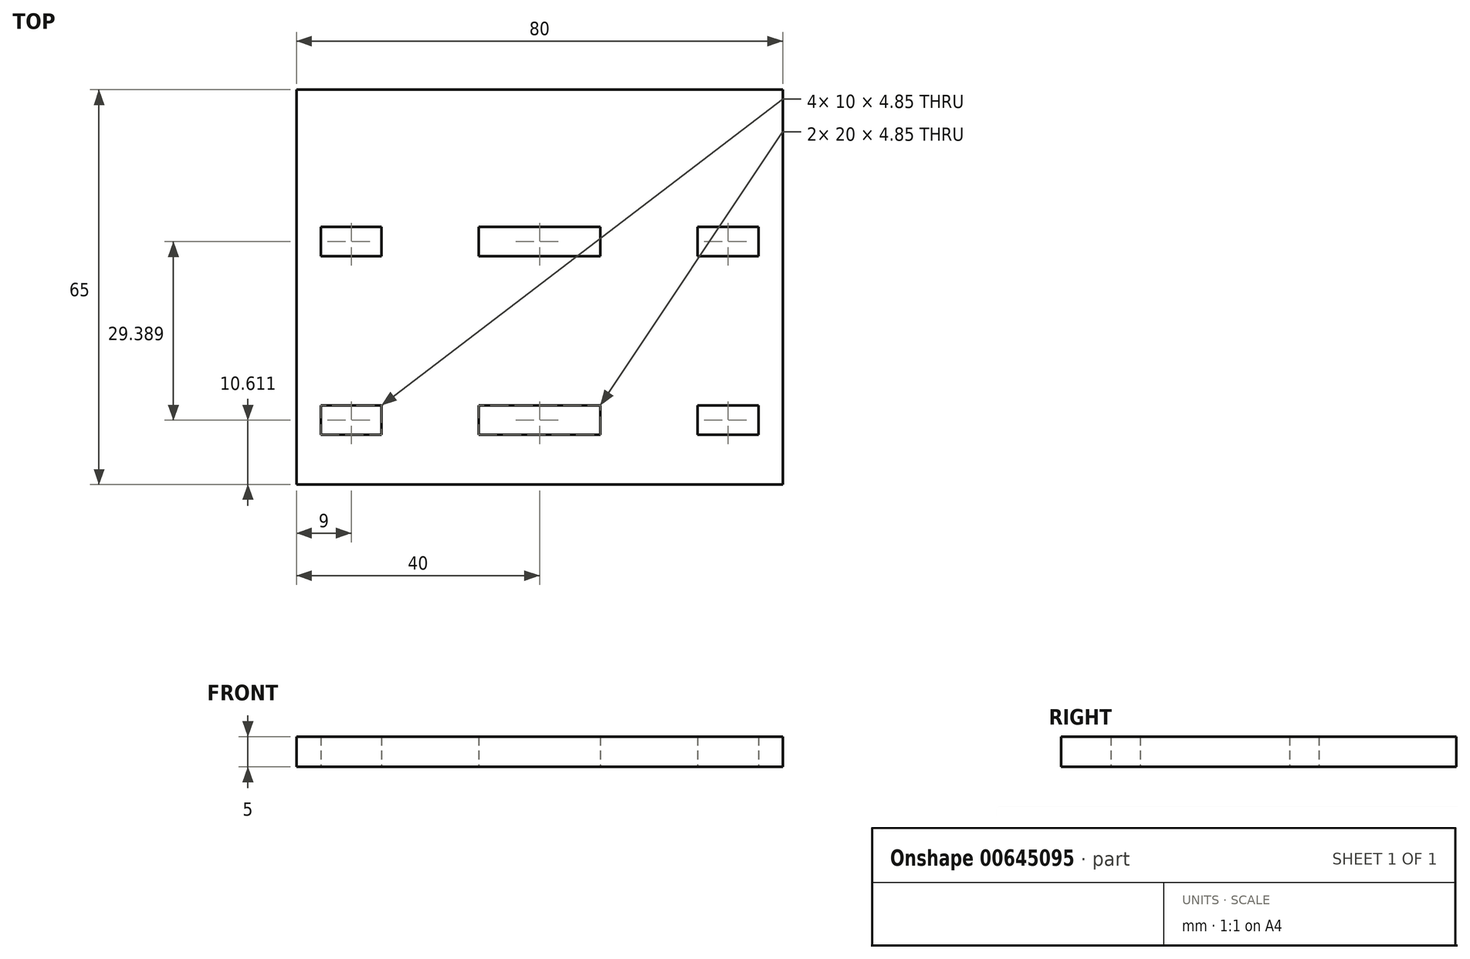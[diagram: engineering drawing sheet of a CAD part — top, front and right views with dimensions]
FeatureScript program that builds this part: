
annotation { "Feature Type Name" : "Feature", "Feature Type Description" : "" }
export const myFeature = defineFeature(function(context is Context, id is Id, definition is map)
    precondition{}
    {
        {
            var Q0;
            Q0=qCreatedBy(makeId("Top.planeOp"),FACE);
            var sketch = newSketch(context, id + "F0", { "sketchPlane" : qUnion([Q0])});
            skLineSegment(sketch, "E0.bottom", {"start": v(40, -25) * mm, "end": v(-40, -25) * mm});
            skLineSegment(sketch, "E0.top", {"start": v(40, 25) * mm, "end": v(-40, 25) * mm});
            skLineSegment(sketch, "E0.left", {"start": v(40, -25) * mm, "end": v(40, 25) * mm});
            skLineSegment(sketch, "E0.right", {"start": v(-40, -25) * mm, "end": v(-40, 25) * mm});
            skPoint(sketch, "E0.middle", {"position": v(0, 0) * mm});
            skLineSegment(sketch, "E1", {"start": v(-40, 0) * mm, "end": v(-31, 0) * mm, "construction": true});
            skLineSegment(sketch, "E2.bottom", {"start": v(10, -2.43) * mm, "end": v(-10, -2.43) * mm});
            skLineSegment(sketch, "E2.top", {"start": v(10, 2.43) * mm, "end": v(-10, 2.43) * mm});
            skLineSegment(sketch, "E2.left", {"start": v(10, -2.43) * mm, "end": v(10, 2.43) * mm});
            skLineSegment(sketch, "E2.right", {"start": v(-10, -2.42) * mm, "end": v(-10, 2.43) * mm});
            skLineSegment(sketch, "E3.bottom", {"start": v(36, 2.43) * mm, "end": v(26, 2.43) * mm});
            skLineSegment(sketch, "E3.top", {"start": v(36, -2.42) * mm, "end": v(26, -2.42) * mm});
            skLineSegment(sketch, "E3.left", {"start": v(36, 2.43) * mm, "end": v(36, -2.42) * mm});
            skLineSegment(sketch, "E3.right", {"start": v(26, 2.43) * mm, "end": v(26, -2.42) * mm});
            skPoint(sketch, "E3.middle", {"position": v(31, 0) * mm});
            skLineSegment(sketch, "E4.bottom", {"start": v(-26, -2.43) * mm, "end": v(-36, -2.43) * mm});
            skLineSegment(sketch, "E4.top", {"start": v(-26, 2.43) * mm, "end": v(-36, 2.43) * mm});
            skLineSegment(sketch, "E4.left", {"start": v(-26, -2.43) * mm, "end": v(-26, 2.43) * mm});
            skLineSegment(sketch, "E4.right", {"start": v(-36, -2.43) * mm, "end": v(-36, 2.43) * mm});
            skPoint(sketch, "E4.middle", {"position": v(-31, 0) * mm});
            skLineSegment(sketch, "E5.trimOffspring", {"start": v(-26, 0) * mm, "end": v(-10, 0) * mm, "construction": true});
            skLineSegment(sketch, "E6.trimOffspring", {"start": v(10, 0) * mm, "end": v(26, 0) * mm, "construction": true});
            skLineSegment(sketch, "E7.trimOffspring", {"start": v(31, 0) * mm, "end": v(40, 0) * mm, "construction": true});
            skLineSegment(sketch, "E8.bottom", {"start": v(-40, -25) * mm, "end": v(40, -25) * mm});
            skLineSegment(sketch, "E8.top", {"start": v(-40, -40) * mm, "end": v(40, -40) * mm});
            skLineSegment(sketch, "E8.left", {"start": v(-40, -25) * mm, "end": v(-40, -40) * mm});
            skLineSegment(sketch, "E8.right", {"start": v(40, -25) * mm, "end": v(40, -40) * mm});
            skLineSegment(sketch, "E9.bottom", {"start": v(-36, -2.43) * mm, "end": v(36, -2.43) * mm, "construction": true});
            skLineSegment(sketch, "E9.top", {"start": v(-36, 2.43) * mm, "end": v(36, 2.43) * mm, "construction": true});
            skLineSegment(sketch, "E9.left", {"start": v(-36, -2.43) * mm, "end": v(-36, 2.43) * mm, "construction": true});
            skLineSegment(sketch, "E9.right", {"start": v(36, 2.43) * mm, "end": v(36, -2.42) * mm, "construction": true});
            skLineSegment(sketch, "E10.top", {"start": v(-36, -27.42) * mm, "end": v(36, -27.42) * mm, "construction": true});
            skLineSegment(sketch, "E10.left", {"start": v(-36, -2.43) * mm, "end": v(-36, -27.42) * mm, "construction": true});
            skLineSegment(sketch, "E10.right", {"start": v(36, -2.43) * mm, "end": v(36, -27.42) * mm, "construction": true});
            skPoint(sketch, "E11.middle", {"position": v(0, -29.39) * mm});
            skLineSegment(sketch, "E12", {"start": v(-40, -29.39) * mm, "end": v(-31, -29.39) * mm, "construction": true});
            skLineSegment(sketch, "E13.bottom", {"start": v(10, -31.81) * mm, "end": v(-10, -31.81) * mm});
            skLineSegment(sketch, "E13.top", {"start": v(10, -26.96) * mm, "end": v(-10, -26.96) * mm});
            skLineSegment(sketch, "E13.left", {"start": v(10, -31.81) * mm, "end": v(10, -26.96) * mm});
            skLineSegment(sketch, "E13.right", {"start": v(-10, -31.81) * mm, "end": v(-10, -26.96) * mm});
            skLineSegment(sketch, "E14.bottom", {"start": v(36, -26.96) * mm, "end": v(26, -26.96) * mm});
            skLineSegment(sketch, "E14.top", {"start": v(36, -31.81) * mm, "end": v(26, -31.81) * mm});
            skLineSegment(sketch, "E14.left", {"start": v(36, -26.96) * mm, "end": v(36, -31.81) * mm});
            skLineSegment(sketch, "E14.right", {"start": v(26, -26.96) * mm, "end": v(26, -31.81) * mm});
            skPoint(sketch, "E14.middle", {"position": v(31, -29.39) * mm});
            skLineSegment(sketch, "E15.bottom", {"start": v(-26, -31.81) * mm, "end": v(-36, -31.81) * mm});
            skLineSegment(sketch, "E15.top", {"start": v(-26, -26.96) * mm, "end": v(-36, -26.96) * mm});
            skLineSegment(sketch, "E15.left", {"start": v(-26, -31.81) * mm, "end": v(-26, -26.96) * mm});
            skLineSegment(sketch, "E15.right", {"start": v(-36, -31.81) * mm, "end": v(-36, -26.96) * mm});
            skPoint(sketch, "E15.middle", {"position": v(-31, -29.39) * mm});
            skLineSegment(sketch, "E16.trimOffspring", {"start": v(-26, -29.39) * mm, "end": v(-10, -29.39) * mm, "construction": true});
            skLineSegment(sketch, "E17.trimOffspring", {"start": v(10, -29.39) * mm, "end": v(26, -29.39) * mm, "construction": true});
            skLineSegment(sketch, "E18.trimOffspring", {"start": v(31, -29.39) * mm, "end": v(40, -29.39) * mm, "construction": true});
            skLineSegment(sketch, "E19.bottom", {"start": v(-36, -31.81) * mm, "end": v(36, -31.81) * mm, "construction": true});
            skLineSegment(sketch, "E19.top", {"start": v(-36, -26.96) * mm, "end": v(36, -26.96) * mm, "construction": true});
            skLineSegment(sketch, "E19.left", {"start": v(-36, -31.81) * mm, "end": v(-36, -26.96) * mm, "construction": true});
            skLineSegment(sketch, "E19.right", {"start": v(36, -26.96) * mm, "end": v(36, -31.81) * mm, "construction": true});
            skSolve(sketch);
        }
        {
            var Q0;
            Q0 = qSketchRegion(id + "F0", true);
            extrude(context, id + "F1", {"entities" : qUnion([Q0]), "depth" : 5 * mm, "offsetDistance" : 25 * mm});
        }
    });
